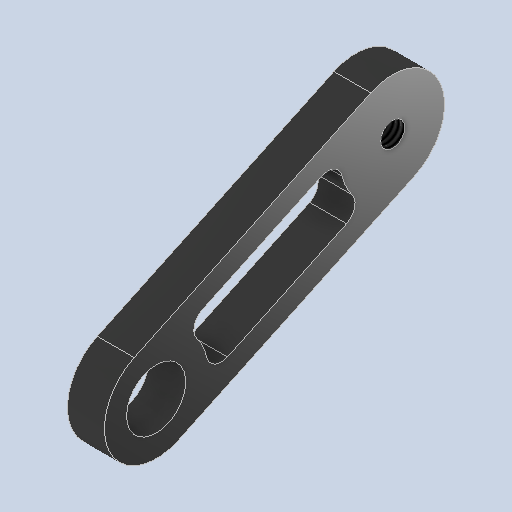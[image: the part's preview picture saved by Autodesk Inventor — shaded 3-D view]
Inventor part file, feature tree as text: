
AUTODESK INVENTOR PART (.ipt)
format: ipt  version: 2024.2 (Build 282272000, 272)  size: 288,256 bytes
history: native  units: mm
features: sketch x2, hole x2, other x1, extrude x1, fillet x1
ambient origin geometry x8: Origin, YZ Plane, XZ Plane, XY Plane, X Axis, Y Axis, Z Axis, Center Point
bodies: Solid1 (feature_tree)
feature tree (7):
  other  "ParallelLinksDriveFrame.ipt"
  sketch  "Sketch2"  dims[d2=5.0mm d3=0.0mm d4=3.242mm d5=8.0mm d6=4.0mm d7=2.0mm d8=90.0deg d9=8.0mm d10=20.594885mm d11=2.0mm d12=8.0mm d13=8.0mm d14=4.0mm d15=2.0mm d16=90.0deg d17=8.0mm d18=20.594885mm]
  extrude  "Extrusion1"  Depth=3.0mm
  hole  "Hole1"  [1 undecoded]
  fillet  "Fillet1"  [1 undecoded]
  hole  "Hole2"  [1 undecoded]
  sketch  "Sketch1"  dims[d0=10.0mm d1=3.0mm]
note: 3 required parameter values undecoded (feature->parameter linkage not recoverable at this tier; creation-order binding heuristic only, values carry confidence <= 0.55)
